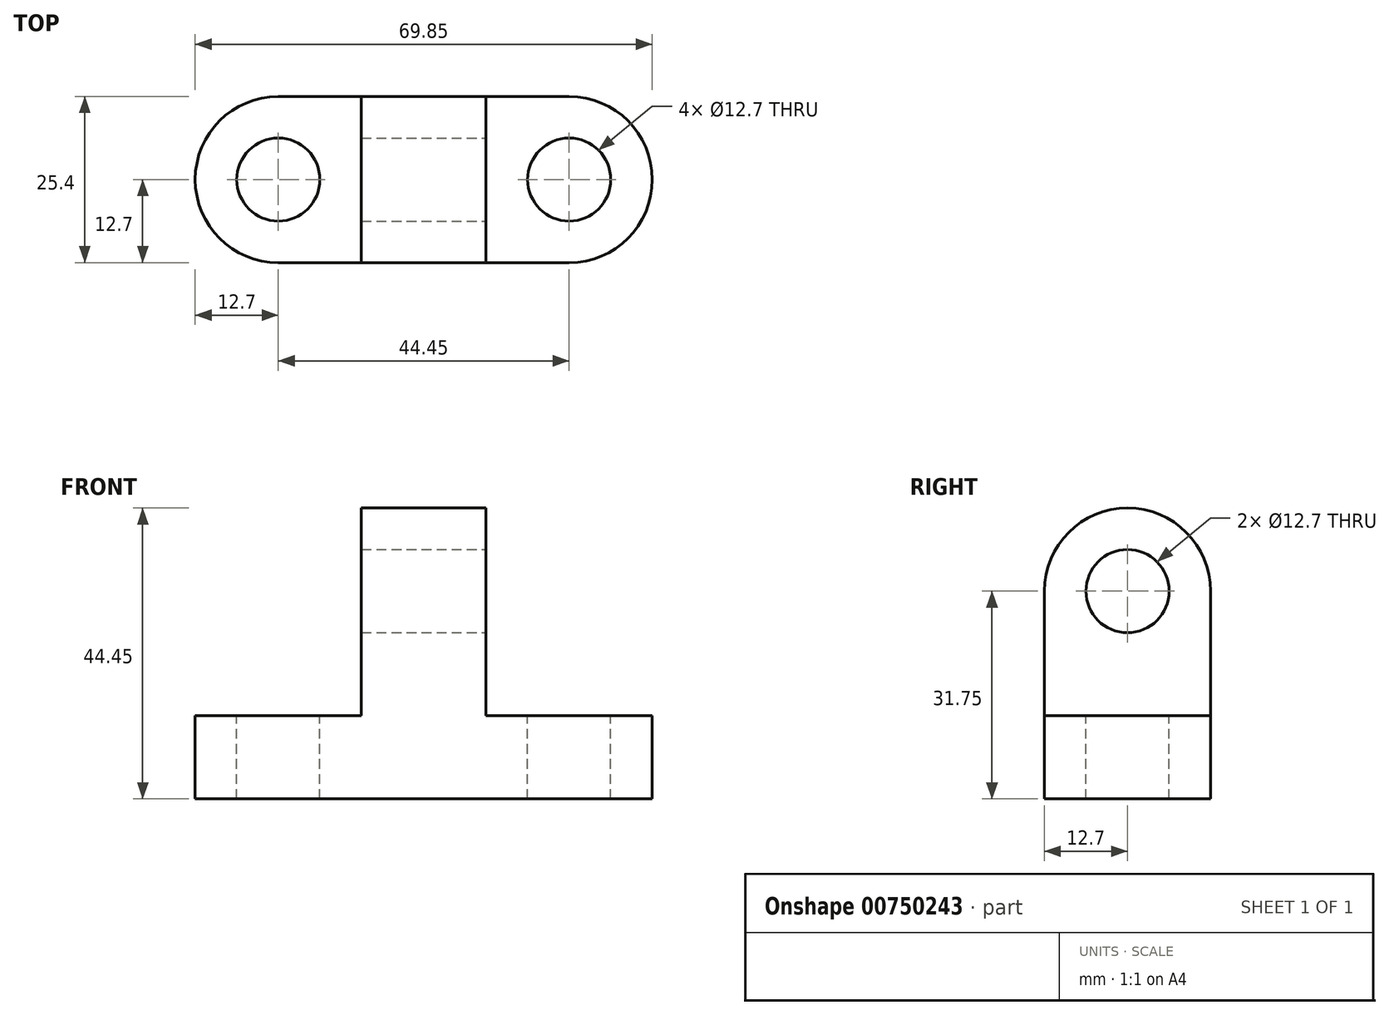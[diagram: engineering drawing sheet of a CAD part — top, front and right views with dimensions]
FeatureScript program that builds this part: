
annotation { "Feature Type Name" : "Feature", "Feature Type Description" : "" }
export const myFeature = defineFeature(function(context is Context, id is Id, definition is map)
    precondition{}
    {
        {
            var Q0;
            Q0=qCreatedBy(makeId("Front.planeOp"),FACE);
            var sketch = newSketch(context, id + "F0", { "sketchPlane" : qUnion([Q0])});
            skLineSegment(sketch, "E0", {"start": v(0, 0) * mm, "end": v(69.85, 0) * mm});
            skLineSegment(sketch, "E1", {"start": v(69.85, 0) * mm, "end": v(69.85, 44.45) * mm});
            skLineSegment(sketch, "E2", {"start": v(69.85, 44.45) * mm, "end": v(0, 44.45) * mm});
            skLineSegment(sketch, "E3", {"start": v(0, 44.45) * mm, "end": v(0, 0) * mm});
            skSolve(sketch);
        }
        {
            var Q0;
            Q0=makeQuery(id+"F0.imprint","IMPRINT",FACE,{"disambiguationData":[TD([[makeQuery(id+"F0.imprint","IMPRINT",EDGE,{"derivedFrom":sQuery(id+"F0.wireOp",EDGE,"E0")}),1.0]])]});
            extrude(context, id + "F1", {"entities" : qUnion([Q0]), "depth" : 25.4 * mm, "offsetDistance" : 25.4 * mm});
        }
        {
            var Q0;
            Q0=makeQuery(id+"F1.opExtrude","CAP_FACE",FACE,{"disambiguationData":[OSD([sQuery(id+"F0.wireOp",EDGE,"E0"),sQuery(id+"F0.wireOp",EDGE,"E1"),sQuery(id+"F0.wireOp",EDGE,"E2"),sQuery(id+"F0.wireOp",EDGE,"E3")])],"isStart":false});
            var sketch = newSketch(context, id + "F2", { "sketchPlane" : qUnion([Q0])});
            skLineSegment(sketch, "E4", {"start": v(0, 12.7) * mm, "end": v(25.4, 12.7) * mm});
            skLineSegment(sketch, "E5", {"start": v(25.4, 12.7) * mm, "end": v(25.4, 44.45) * mm});
            skLineSegment(sketch, "E6", {"start": v(25.4, 44.45) * mm, "end": v(44.45, 44.45) * mm});
            skLineSegment(sketch, "E7", {"start": v(44.45, 44.45) * mm, "end": v(44.45, 12.7) * mm});
            skLineSegment(sketch, "E8", {"start": v(44.45, 12.7) * mm, "end": v(69.85, 12.7) * mm});
            skLineSegment(sketch, "E9", {"start": v(69.85, 12.7) * mm, "end": v(69.85, 0) * mm});
            skLineSegment(sketch, "E10", {"start": v(69.85, 0) * mm, "end": v(0, 0) * mm});
            skLineSegment(sketch, "E11", {"start": v(0, 0) * mm, "end": v(0, 12.7) * mm});
            skSolve(sketch);
        }
        {
            var Q0;
            {var subQ0=sQuery(id+"F2.wireOp",EDGE,"E4");Q0=makeQuery(id+"F2.imprint","IMPRINT",FACE,{"disambiguationData":[TD([[makeQuery(id+"F2.imprint","IMPRINT",EDGE,{"derivedFrom":subQ0}),1.0]])]});}
            var Q1;
            {var subQ0=sQuery(id+"F2.wireOp",EDGE,"E7");Q1=makeQuery(id+"F2.imprint","IMPRINT",FACE,{"disambiguationData":[TD([[makeQuery(id+"F2.imprint","IMPRINT",EDGE,{"derivedFrom":subQ0}),1.0]])]});}
            extrude(context, id + "F3", {"entities" : qUnion([Q0, Q1]), "operationType" : NewBodyOperationType.REMOVE, "oppositeDirection" : true, "depth" : 25.4 * mm, "offsetDistance" : 25.4 * mm});
        }
        {
            var Q0;
            Q0=makeQuery(id+"F3.boolean.opBoolean","COPY",FACE,{"derivedFrom":makeQuery(id+"F3.opExtrude","SWEPT_FACE",FACE,{"disambiguationData":[OSD([sQuery(id+"F2.wireOp",EDGE,"E7")])]})});
            var sketch = newSketch(context, id + "F4", { "sketchPlane" : qUnion([Q0])});
            skArc(sketch, "E12", {"start": v(0, 31.75) * mm, "mid": v(-12.7, 44.45) * mm, "end": v(-25.4, 31.75) * mm});
            skSolve(sketch);
        }
        {
            var Q0;
            {var subQ0=sQuery(id+"F4.wireOp",EDGE,"E12");var subQ1=sQuery(id+"F2.wireOp",EDGE,"E7");var subQ2=makeQuery(id+"F3.boolean.opBoolean","COPY",EDGE,{"derivedFrom":makeQuery(id+"F3.opExtrude","CAP_EDGE",EDGE,{"disambiguationData":[OSD([subQ1])],"isStart":true})});var subQ3=makeQuery(id+"F4.imprint","INTERSECT",VERTEX,{"derivedFrom":[subQ2,subQ0]});Q0=makeQuery(id+"F4.imprint","IMPRINT",FACE,{"disambiguationData":[TD([[makeQuery(id+"F4.imprint","IMPRINT",EDGE,{"disambiguationData":[TD([[subQ3,1.0]])],"derivedFrom":subQ0}),-1.0]])]});}
            var Q1;
            {var subQ0=sQuery(id+"F4.wireOp",EDGE,"E12");var subQ1=sQuery(id+"F2.wireOp",EDGE,"E7");var subQ2=makeQuery(id+"F3.boolean.opBoolean","COPY",EDGE,{"derivedFrom":makeQuery(id+"F3.opExtrude","CAP_EDGE",EDGE,{"disambiguationData":[OSD([subQ1])],"isStart":false})});var subQ3=makeQuery(id+"F4.imprint","INTERSECT",VERTEX,{"derivedFrom":[subQ2,subQ0]});Q1=makeQuery(id+"F4.imprint","IMPRINT",FACE,{"disambiguationData":[TD([[makeQuery(id+"F4.imprint","IMPRINT",EDGE,{"disambiguationData":[TD([[subQ3,-1.0]])],"derivedFrom":subQ0}),-1.0]])]});}
            extrude(context, id + "F5", {"entities" : qUnion([Q0, Q1]), "operationType" : NewBodyOperationType.REMOVE, "oppositeDirection" : true, "depth" : 25.4 * mm, "offsetDistance" : 25.4 * mm});
        }
        {
            var Q0;
            Q0=makeQuery(id+"F3.boolean.opBoolean","COPY",FACE,{"derivedFrom":makeQuery(id+"F3.opExtrude","SWEPT_FACE",FACE,{"disambiguationData":[OSD([sQuery(id+"F2.wireOp",EDGE,"E7")])]})});
            var sketch = newSketch(context, id + "F6", { "sketchPlane" : qUnion([Q0])});
            skCircle(sketch, "E13", {"center": v(-12.7, 31.75) * mm, "radius": 6.35 * mm});
            skSolve(sketch);
        }
        {
            var Q0;
            Q0=makeQuery(id+"F6.imprint","IMPRINT",FACE,{"disambiguationData":[TD([[makeQuery(id+"F6.imprint","IMPRINT",EDGE,{"derivedFrom":sQuery(id+"F6.wireOp",EDGE,"E13")}),1.0]])]});
            extrude(context, id + "F7", {"entities" : qUnion([Q0]), "operationType" : NewBodyOperationType.REMOVE, "oppositeDirection" : true, "depth" : 25.4 * mm, "offsetDistance" : 25.4 * mm});
        }
        {
            var Q0;
            Q0=makeQuery(id+"F3.boolean.opBoolean","COPY",FACE,{"derivedFrom":makeQuery(id+"F3.opExtrude","SWEPT_FACE",FACE,{"disambiguationData":[OSD([sQuery(id+"F2.wireOp",EDGE,"E8")])]})});
            var sketch = newSketch(context, id + "F8", { "sketchPlane" : qUnion([Q0])});
            skArc(sketch, "E14", {"start": v(12.7, 0) * mm, "mid": v(0, -12.7) * mm, "end": v(12.7, -25.4) * mm});
            skPoint(sketch, "E14.endSnap0", {"position": v(57.15, -25.4) * mm});
            skArc(sketch, "E15", {"start": v(57.15, -25.4) * mm, "mid": v(69.85, -12.7) * mm, "end": v(57.15, 0) * mm});
            skSolve(sketch);
        }
        {
            var Q0;
            {var subQ0=sQuery(id+"F8.wireOp",EDGE,"E15");var subQ1=sQuery(id+"F2.wireOp",EDGE,"E8");var subQ2=makeQuery(id+"F3.boolean.opBoolean","COPY",EDGE,{"derivedFrom":makeQuery(id+"F3.opExtrude","CAP_EDGE",EDGE,{"disambiguationData":[OSD([subQ1])],"isStart":false})});var subQ3=makeQuery(id+"F8.imprint","INTERSECT",VERTEX,{"derivedFrom":[subQ2,subQ0]});Q0=makeQuery(id+"F8.imprint","IMPRINT",FACE,{"disambiguationData":[TD([[makeQuery(id+"F8.imprint","IMPRINT",EDGE,{"disambiguationData":[TD([[subQ3,1.0]])],"derivedFrom":subQ0}),-1.0]])]});}
            var Q1;
            {var subQ0=sQuery(id+"F8.wireOp",EDGE,"E15");var subQ1=sQuery(id+"F2.wireOp",EDGE,"E8");var subQ2=makeQuery(id+"F3.boolean.opBoolean","COPY",EDGE,{"derivedFrom":makeQuery(id+"F3.opExtrude","CAP_EDGE",EDGE,{"disambiguationData":[OSD([subQ1])],"isStart":true})});var subQ3=makeQuery(id+"F8.imprint","INTERSECT",VERTEX,{"derivedFrom":[subQ2,subQ0]});Q1=makeQuery(id+"F8.imprint","IMPRINT",FACE,{"disambiguationData":[TD([[makeQuery(id+"F8.imprint","IMPRINT",EDGE,{"disambiguationData":[TD([[subQ3,-1.0]])],"derivedFrom":subQ0}),-1.0]])]});}
            extrude(context, id + "F9", {"entities" : qUnion([Q0, Q1]), "operationType" : NewBodyOperationType.REMOVE, "oppositeDirection" : true, "depth" : 25.4 * mm, "offsetDistance" : 25.4 * mm});
        }
        {
            var Q0;
            Q0=makeQuery(id+"F3.boolean.opBoolean","COPY",FACE,{"derivedFrom":makeQuery(id+"F3.opExtrude","SWEPT_FACE",FACE,{"disambiguationData":[OSD([sQuery(id+"F2.wireOp",EDGE,"E4")])]})});
            var sketch = newSketch(context, id + "F10", { "sketchPlane" : qUnion([Q0])});
            skArc(sketch, "E16", {"start": v(12.7, 0) * mm, "mid": v(0, -12.7) * mm, "end": v(12.7, -25.4) * mm});
            skSolve(sketch);
        }
        {
            var Q0;
            {var subQ0=sQuery(id+"F10.wireOp",EDGE,"E16");var subQ1=sQuery(id+"F2.wireOp",EDGE,"E4");var subQ2=makeQuery(id+"F3.boolean.opBoolean","COPY",EDGE,{"derivedFrom":makeQuery(id+"F3.opExtrude","CAP_EDGE",EDGE,{"disambiguationData":[OSD([subQ1])],"isStart":false})});var subQ3=makeQuery(id+"F10.imprint","INTERSECT",VERTEX,{"derivedFrom":[subQ2,subQ0]});Q0=makeQuery(id+"F10.imprint","IMPRINT",FACE,{"disambiguationData":[TD([[makeQuery(id+"F10.imprint","IMPRINT",EDGE,{"disambiguationData":[TD([[subQ3,-1.0]])],"derivedFrom":subQ0}),-1.0]])]});}
            var Q1;
            {var subQ0=sQuery(id+"F10.wireOp",EDGE,"E16");var subQ1=sQuery(id+"F2.wireOp",EDGE,"E4");var subQ2=makeQuery(id+"F3.boolean.opBoolean","COPY",EDGE,{"derivedFrom":makeQuery(id+"F3.opExtrude","CAP_EDGE",EDGE,{"disambiguationData":[OSD([subQ1])],"isStart":true})});var subQ3=makeQuery(id+"F10.imprint","INTERSECT",VERTEX,{"derivedFrom":[subQ2,subQ0]});Q1=makeQuery(id+"F10.imprint","IMPRINT",FACE,{"disambiguationData":[TD([[makeQuery(id+"F10.imprint","IMPRINT",EDGE,{"disambiguationData":[TD([[subQ3,1.0]])],"derivedFrom":subQ0}),-1.0]])]});}
            extrude(context, id + "F11", {"entities" : qUnion([Q0, Q1]), "operationType" : NewBodyOperationType.REMOVE, "oppositeDirection" : true, "depth" : 25.4 * mm, "offsetDistance" : 25.4 * mm});
        }
        {
            var Q0;
            Q0=makeQuery(id+"F3.boolean.opBoolean","COPY",FACE,{"derivedFrom":makeQuery(id+"F3.opExtrude","SWEPT_FACE",FACE,{"disambiguationData":[OSD([sQuery(id+"F2.wireOp",EDGE,"E4")])]})});
            var sketch = newSketch(context, id + "F12", { "sketchPlane" : qUnion([Q0])});
            skCircle(sketch, "E17", {"center": v(12.7, -12.7) * mm, "radius": 6.35 * mm});
            skPoint(sketch, "E17.centerSnap0", {"position": v(0, -12.7) * mm});
            skCircle(sketch, "E18", {"center": v(57.15, -12.7) * mm, "radius": 6.35 * mm});
            skPoint(sketch, "E18.centerSnap0", {"position": v(25.4, -12.7) * mm});
            skSolve(sketch);
        }
        {
            var Q0;
            Q0=makeQuery(id+"F12.imprint","IMPRINT",FACE,{"disambiguationData":[TD([[makeQuery(id+"F12.imprint","IMPRINT",EDGE,{"derivedFrom":sQuery(id+"F12.wireOp",EDGE,"E17")}),1.0]])]});
            var Q1;
            Q1=makeQuery(id+"F12.imprint","IMPRINT",FACE,{"disambiguationData":[TD([[makeQuery(id+"F12.imprint","IMPRINT",EDGE,{"derivedFrom":sQuery(id+"F12.wireOp",EDGE,"E18")}),1.0]])]});
            extrude(context, id + "F13", {"entities" : qUnion([Q0, Q1]), "operationType" : NewBodyOperationType.REMOVE, "oppositeDirection" : true, "depth" : 25.4 * mm, "offsetDistance" : 25.4 * mm});
        }
    });
